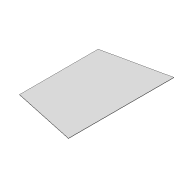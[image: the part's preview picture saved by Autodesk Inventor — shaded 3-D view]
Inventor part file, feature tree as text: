
AUTODESK INVENTOR PART (.ipt)
format: ipt  version: 2021 (Build 250183000, 183)  size: 72,192 bytes
history: native  units: in
note: dims shown in document units (in); Inventor stores cm internally (conversion verified against a paired STEP export)
features: extrude x1, sketch x1
ambient origin geometry x8: Origin, YZ Plane, XZ Plane, XY Plane, X Axis, Y Axis, Z Axis, Center Point
bodies: Solid1 (feature_tree)
feature tree (2):
  extrude  "Extrusion1"  [1 undecoded]
  sketch  "Sketch2"  dims[d8=0.063in d9=0.0in]
note: 1 required parameter value undecoded (feature->parameter linkage not recoverable at this tier; creation-order binding heuristic only, values carry confidence <= 0.55)
